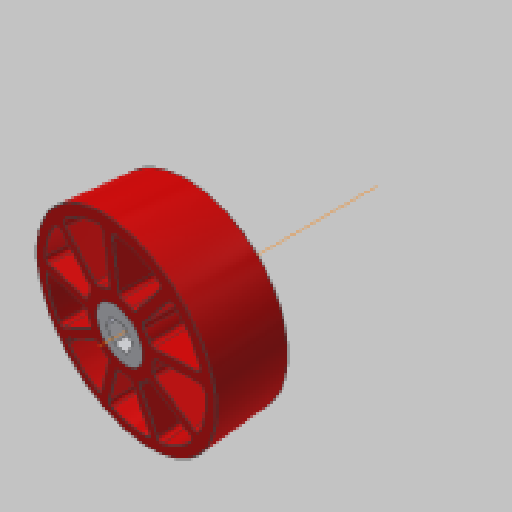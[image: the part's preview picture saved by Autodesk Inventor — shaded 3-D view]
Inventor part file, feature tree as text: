
AUTODESK INVENTOR PART (.ipt)
format: ipt  version: 2023.5 (Build 275446000, 446)  size: 1,046,528 bytes
history: native  units: in
note: dims shown in document units (in); Inventor stores cm internally (conversion verified against a paired STEP export)
features: other x3, plane x1
ambient origin geometry x8: Origin, YZ Plane, XZ Plane, XY Plane, X Axis, Y Axis, Z Axis, Center Point
bodies: Solid1 (feature_tree), Solid2 (feature_tree)
feature tree (4):
  plane  "Work Plane1"
  other  "Work Axis1"
  other  "3IN Molded Compliant Wheel Tread VER2-1-solid1"
  other  "am-3947-1000 375H x 1000IN Spacer-1-solid1"
